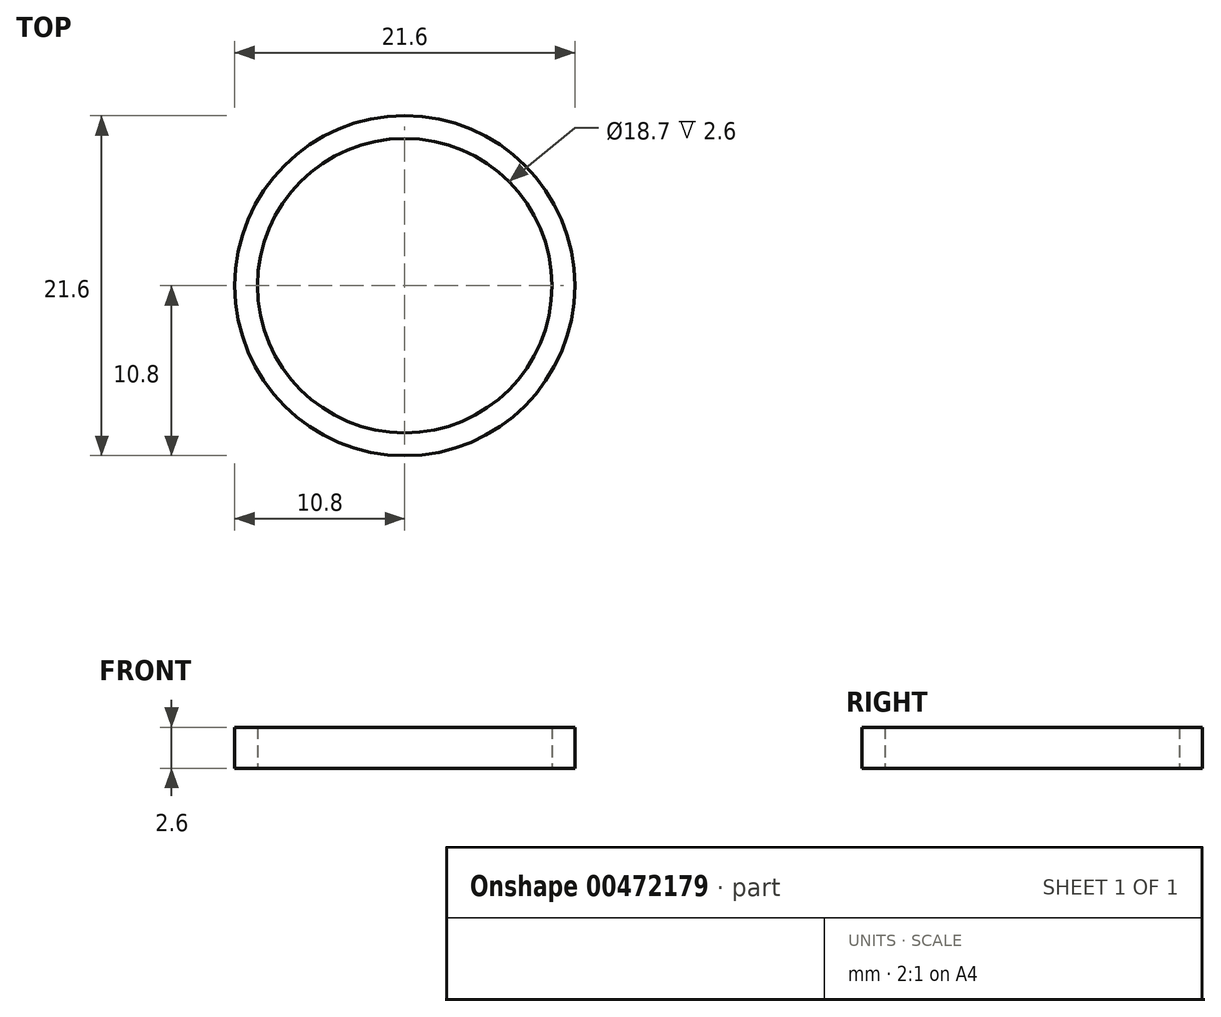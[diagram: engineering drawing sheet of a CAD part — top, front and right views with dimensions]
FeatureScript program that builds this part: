
annotation { "Feature Type Name" : "Feature", "Feature Type Description" : "" }
export const myFeature = defineFeature(function(context is Context, id is Id, definition is map)
    precondition{}
    {
        {
            var Q0;
            Q0=qCreatedBy(makeId("Top.planeOp"),FACE);
            var sketch = newSketch(context, id + "F0", { "sketchPlane" : qUnion([Q0])});
            skCircle(sketch, "E0", {"center": v(0, 0) * mm, "radius": 10.8 * mm});
            skCircle(sketch, "E1", {"center": v(0, 0) * mm, "radius": 9.35 * mm});
            skSolve(sketch);
        }
        {
            var Q0;
            Q0=makeQuery(id+"F0.imprint","IMPRINT",FACE,{"disambiguationData":[TD([[makeQuery(id+"F0.imprint","IMPRINT",EDGE,{"derivedFrom":sQuery(id+"F0.wireOp",EDGE,"E0")}),1.0]])]});
            extrude(context, id + "F1", {"entities" : qUnion([Q0]), "depth" : 2.6 * mm});
        }
    });
